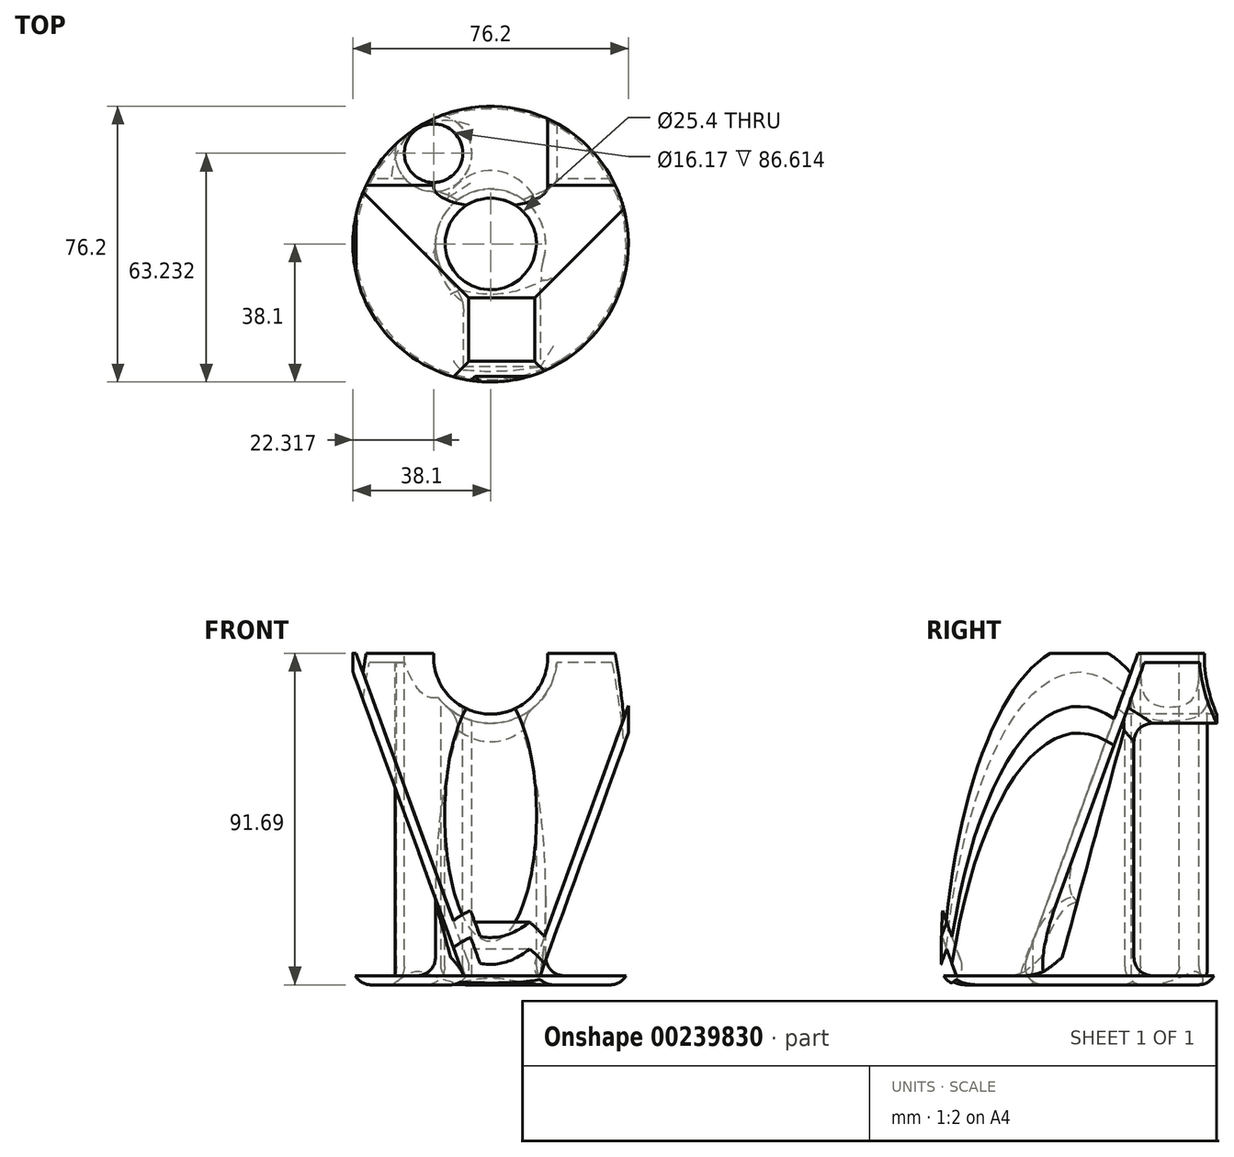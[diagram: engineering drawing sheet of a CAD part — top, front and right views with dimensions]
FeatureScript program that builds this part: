
annotation { "Feature Type Name" : "Feature", "Feature Type Description" : "" }
export const myFeature = defineFeature(function(context is Context, id is Id, definition is map)
    precondition{}
    {
        {
            var Q0;
            Q0=qCreatedBy(makeId("Top.planeOp"),FACE);
            var sketch = newSketch(context, id + "F0", { "sketchPlane" : qUnion([Q0])});
            skCircle(sketch, "E0", {"center": v(0, 0) * mm, "radius": 38.1 * mm});
            skSolve(sketch);
        }
        {
            var Q0;
            Q0=makeQuery(id+"F0.imprint","IMPRINT",FACE,{"disambiguationData":[TD([[makeQuery(id+"F0.imprint","IMPRINT",EDGE,{"derivedFrom":sQuery(id+"F0.wireOp",EDGE,"E0")}),1.0]])]});
            extrude(context, id + "F1", {"entities" : qUnion([Q0]), "depth" : 66.3 * mm});
        }
        {
            var Q0;
            Q0=makeQuery(id+"F1.opExtrude","CAP_FACE",FACE,{"disambiguationData":[OSD([sQuery(id+"F0.wireOp",EDGE,"E0")])],"isStart":false});
            var sketch = newSketch(context, id + "F2", { "sketchPlane" : qUnion([Q0])});
            skCircle(sketch, "E1", {"center": v(0, 0) * mm, "radius": 12.7 * mm});
            skSolve(sketch);
        }
        {
            var Q0;
            Q0=makeQuery(id+"F2.imprint","IMPRINT",FACE,{"disambiguationData":[TD([[makeQuery(id+"F2.imprint","IMPRINT",EDGE,{"derivedFrom":sQuery(id+"F2.wireOp",EDGE,"E1")}),-1.0]])]});
            var sketch = newSketch(context, id + "F3", { "sketchPlane" : qUnion([Q0])});
            skCircle(sketch, "E2", {"center": v(0, 0) * mm, "radius": 12.7 * mm});
            skSolve(sketch);
        }
        {
            var Q0;
            Q0 = qSketchRegion(id + "F3", true);
            extrude(context, id + "F4", {"entities" : qUnion([Q0]), "operationType" : NewBodyOperationType.REMOVE, "oppositeDirection" : true, "depth" : 90.42 * mm});
        }
        {
            var Q0;
            Q0=makeQuery(id+"F2.imprint","IMPRINT",FACE,{"disambiguationData":[TD([[makeQuery(id+"F2.imprint","IMPRINT",EDGE,{"derivedFrom":sQuery(id+"F2.wireOp",EDGE,"E1")}),-1.0]])]});
            var sketch = newSketch(context, id + "F5", { "sketchPlane" : qUnion([Q0])});
            skCircle(sketch, "E3", {"center": v(-15.78, 25.13) * mm, "radius": 8.08 * mm});
            skSolve(sketch);
        }
        {
            var Q0;
            Q0 = qSketchRegion(id + "F5", true);
            extrude(context, id + "F6", {"entities" : qUnion([Q0]), "operationType" : NewBodyOperationType.REMOVE, "oppositeDirection" : true, "depth" : 82.55 * mm});
        }
        {
            var Q0;
            Q0=qCreatedBy(makeId("Front.planeOp"),FACE);
            var sketch = newSketch(context, id + "F7", { "sketchPlane" : qUnion([Q0])});
            skCircle(sketch, "E4", {"center": v(0, 65.23) * mm, "radius": 15.79 * mm});
            skSolve(sketch);
        }
        {
            var Q0;
            Q0 = qSketchRegion(id + "F7", true);
            extrude(context, id + "F8", {"entities" : qUnion([Q0]), "operationType" : NewBodyOperationType.REMOVE, "oppositeDirection" : true, "depth" : 77.22 * mm});
        }
        {
            var Q0;
            Q0=makeQuery(id+"F1.opExtrude","CAP_FACE",FACE,{"disambiguationData":[OSD([sQuery(id+"F0.wireOp",EDGE,"E0")])],"isStart":true});
            var sketch = newSketch(context, id + "F9", { "sketchPlane" : qUnion([Q0])});
            skLineSegment(sketch, "E5.bottom", {"start": v(8.26, 21.73) * mm, "end": v(28.17, 21.73) * mm});
            skLineSegment(sketch, "E5.top", {"start": v(8.26, 11.05) * mm, "end": v(28.17, 11.05) * mm});
            skLineSegment(sketch, "E5.left", {"start": v(8.26, 21.73) * mm, "end": v(8.26, 11.05) * mm});
            skLineSegment(sketch, "E5.right", {"start": v(28.17, 21.73) * mm, "end": v(28.17, 11.05) * mm});
            skSolve(sketch);
        }
        {
            var Q0;
            Q0=makeQuery(id+"F1.opExtrude","CAP_FACE",FACE,{"disambiguationData":[OSD([sQuery(id+"F0.wireOp",EDGE,"E0")])],"isStart":true});
            var Q1;
            Q1=makeQuery(id+"F9.imprint","IMPRINT",FACE,{"disambiguationData":[TD([[makeQuery(id+"F9.imprint","IMPRINT",EDGE,{"derivedFrom":sQuery(id+"F9.wireOp",EDGE,"E5.bottom")}),1.0]])]});
            var Q2;
            Q2=makeQuery(id+"F9.imprint","IMPRINT",FACE,{"disambiguationData":[TD([[makeQuery(id+"F9.imprint","IMPRINT",EDGE,{"derivedFrom":sQuery(id+"F9.wireOp",EDGE,"E5.bottom")}),-1.0]])]});
            extrude(context, id + "F10", {"entities" : qUnion([Q0, Q1, Q2]), "operationType" : NewBodyOperationType.ADD, "depth" : 25.4 * mm});
        }
        {
            var Q0;
            Q0=makeQuery(id+"F10.opExtrude","CAP_FACE",FACE,{"disambiguationData":[OSD([sQuery(id+"F0.wireOp",EDGE,"E0")])],"isStart":false});
            var sketch = newSketch(context, id + "F11", { "sketchPlane" : qUnion([Q0])});
            skLineSegment(sketch, "E6.bottom", {"start": v(1.94, 48.69) * mm, "end": v(8.01, 48.69) * mm});
            skLineSegment(sketch, "E6.top", {"start": v(1.94, 42.86) * mm, "end": v(8.01, 42.86) * mm});
            skLineSegment(sketch, "E6.left", {"start": v(1.94, 48.69) * mm, "end": v(1.94, 42.86) * mm});
            skLineSegment(sketch, "E6.right", {"start": v(8.01, 48.69) * mm, "end": v(8.01, 42.86) * mm});
            skLineSegment(sketch, "E7.bottom", {"start": v(-3.89, 30.23) * mm, "end": v(10.04, 30.23) * mm});
            skLineSegment(sketch, "E7.top", {"start": v(-3.89, 17.04) * mm, "end": v(10.04, 17.04) * mm});
            skLineSegment(sketch, "E7.left", {"start": v(-3.89, 30.23) * mm, "end": v(-3.89, 17.04) * mm});
            skLineSegment(sketch, "E7.right", {"start": v(10.04, 30.23) * mm, "end": v(10.04, 17.04) * mm});
            skSolve(sketch);
        }
        {
            var Q0;
            Q0=makeQuery(id+"F11.imprint","IMPRINT",FACE,{"disambiguationData":[TD([[makeQuery(id+"F11.imprint","IMPRINT",EDGE,{"derivedFrom":sQuery(id+"F11.wireOp",EDGE,"E6.bottom")}),-1.0]])]});
            var Q1;
            Q1=makeQuery(id+"F11.imprint","IMPRINT",FACE,{"disambiguationData":[TD([[makeQuery(id+"F11.imprint","IMPRINT",EDGE,{"derivedFrom":sQuery(id+"F11.wireOp",EDGE,"E7.bottom")}),-1.0]])]});
            extrude(context, id + "F12", {"entities" : qUnion([Q0, Q1]), "operationType" : NewBodyOperationType.REMOVE, "oppositeDirection" : true, "depth" : 96.27 * mm, "hasDraft" : true, "draftAngle" : 20 * degree});
        }
        {
            var Q0;
            {var subQ0=sQuery(id+"F0.wireOp",EDGE,"E0");Q0=makeQuery(id+"F10.boolean.opBoolean","MERGE",FACE,{"derivedFrom":[makeQuery(id+"F1.opExtrude","SWEPT_FACE",FACE,{"disambiguationData":[OSD([subQ0])]}),makeQuery(id+"F10.opExtrude","SWEPT_FACE",FACE,{"disambiguationData":[OSD([subQ0]),TDD([makeQuery(id+"F1.opExtrude","CAP_EDGE",EDGE,{"disambiguationData":[OSD([subQ0])],"isStart":true})])]})]});}
            shell(context, id + "F13", {"entities" : qUnion([Q0]), "thickness" : 2.54 * mm});
        }
        {
            var Q0;
            Q0=makeQuery(id+"F10.opExtrude","CAP_FACE",FACE,{"disambiguationData":[OSD([sQuery(id+"F0.wireOp",EDGE,"E0")])],"isStart":false});
            fillet(context, id + "F14", {"entities" : qUnion([Q0]), "radius" : 5.08 * mm, "tangentPropagation" : true, "allowEdgeOverflow" : false});
        }
        {
            var Q0;
            Q0=makeQuery(id+"F13.opShell","OFFSET_FACE",FACE,{"disambiguationData":[OSD([sQuery(id+"F0.wireOp",EDGE,"E0"),sQuery(id+"F3.wireOp",EDGE,"E2")])]});
            fillet(context, id + "F15", {"entities" : qUnion([Q0]), "radius" : 5.08 * mm, "tangentPropagation" : true, "allowEdgeOverflow" : false});
        }
    });
